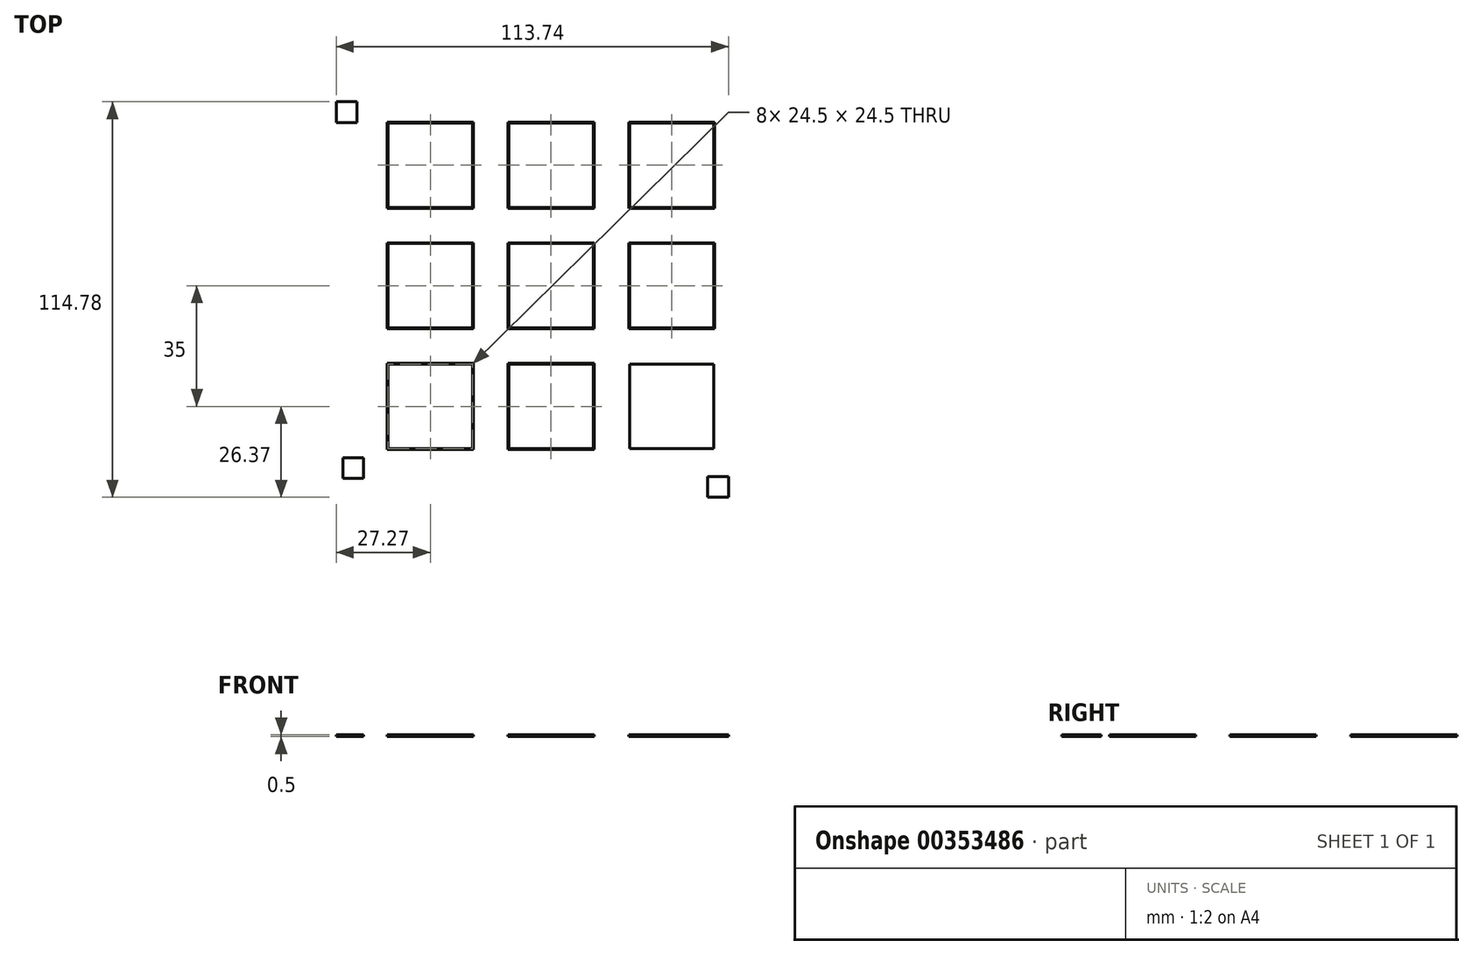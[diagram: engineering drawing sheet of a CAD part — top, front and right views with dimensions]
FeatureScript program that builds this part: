
annotation { "Feature Type Name" : "Feature", "Feature Type Description" : "" }
export const myFeature = defineFeature(function(context is Context, id is Id, definition is map)
    precondition{}
    {
        {
            var Q0;
            Q0=qCreatedBy(makeId("Top.planeOp"),FACE);
            var sketch = newSketch(context, id + "F0", { "sketchPlane" : qUnion([Q0])});
            skLineSegment(sketch, "E0.bottom", {"start": v(-22.5, -12.5) * mm, "end": v(-47.5, -12.5) * mm});
            skLineSegment(sketch, "E0.top", {"start": v(-22.5, 12.5) * mm, "end": v(-47.5, 12.5) * mm});
            skLineSegment(sketch, "E0.left", {"start": v(-22.5, -12.5) * mm, "end": v(-22.5, 12.5) * mm});
            skLineSegment(sketch, "E0.right", {"start": v(-47.5, -12.5) * mm, "end": v(-47.5, 12.5) * mm});
            skPoint(sketch, "E0.middle", {"position": v(-35, 0) * mm});
            skLineSegment(sketch, "E1.bottom", {"start": v(-47.25, 12.25) * mm, "end": v(-22.75, 12.25) * mm});
            skLineSegment(sketch, "E1.top", {"start": v(-47.25, -12.25) * mm, "end": v(-22.75, -12.25) * mm});
            skLineSegment(sketch, "E1.left", {"start": v(-47.25, 12.25) * mm, "end": v(-47.25, -12.25) * mm});
            skLineSegment(sketch, "E1.right", {"start": v(-22.75, 12.25) * mm, "end": v(-22.75, -12.25) * mm});
            skLineSegment(sketch, "E2.bottom", {"start": v(12.5, 22.5) * mm, "end": v(-12.5, 22.5) * mm});
            skLineSegment(sketch, "E2.top", {"start": v(12.5, 47.5) * mm, "end": v(-12.5, 47.5) * mm});
            skLineSegment(sketch, "E2.left", {"start": v(12.5, 22.5) * mm, "end": v(12.5, 47.5) * mm});
            skLineSegment(sketch, "E2.right", {"start": v(-12.5, 22.5) * mm, "end": v(-12.5, 47.5) * mm});
            skPoint(sketch, "E2.middle", {"position": v(0, 35) * mm});
            skLineSegment(sketch, "E3.bottom", {"start": v(-12.25, 47.25) * mm, "end": v(12.25, 47.25) * mm});
            skLineSegment(sketch, "E3.top", {"start": v(-12.25, 22.75) * mm, "end": v(12.25, 22.75) * mm});
            skLineSegment(sketch, "E3.left", {"start": v(-12.25, 47.25) * mm, "end": v(-12.25, 22.75) * mm});
            skLineSegment(sketch, "E3.right", {"start": v(12.25, 47.25) * mm, "end": v(12.25, 22.75) * mm});
            skLineSegment(sketch, "E4.bottom", {"start": v(-22.5, 22.5) * mm, "end": v(-47.5, 22.5) * mm});
            skLineSegment(sketch, "E4.top", {"start": v(-22.5, 47.5) * mm, "end": v(-47.5, 47.5) * mm});
            skLineSegment(sketch, "E4.left", {"start": v(-22.5, 22.5) * mm, "end": v(-22.5, 47.5) * mm});
            skLineSegment(sketch, "E4.right", {"start": v(-47.5, 22.5) * mm, "end": v(-47.5, 47.5) * mm});
            skPoint(sketch, "E4.middle", {"position": v(-35, 35) * mm});
            skLineSegment(sketch, "E5.bottom", {"start": v(-47.25, 47.25) * mm, "end": v(-22.75, 47.25) * mm});
            skLineSegment(sketch, "E5.top", {"start": v(-47.25, 22.75) * mm, "end": v(-22.75, 22.75) * mm});
            skLineSegment(sketch, "E5.left", {"start": v(-47.25, 47.25) * mm, "end": v(-47.25, 22.75) * mm});
            skLineSegment(sketch, "E5.right", {"start": v(-22.75, 47.25) * mm, "end": v(-22.75, 22.75) * mm});
            skLineSegment(sketch, "E6.bottom", {"start": v(12.5, -12.5) * mm, "end": v(-12.5, -12.5) * mm});
            skLineSegment(sketch, "E6.top", {"start": v(12.5, 12.5) * mm, "end": v(-12.5, 12.5) * mm});
            skLineSegment(sketch, "E6.left", {"start": v(12.5, -12.5) * mm, "end": v(12.5, 12.5) * mm});
            skLineSegment(sketch, "E6.right", {"start": v(-12.5, -12.5) * mm, "end": v(-12.5, 12.5) * mm});
            skPoint(sketch, "E6.middle", {"position": v(0, 0) * mm});
            skLineSegment(sketch, "E7.bottom", {"start": v(-12.25, 12.25) * mm, "end": v(12.25, 12.25) * mm});
            skLineSegment(sketch, "E7.top", {"start": v(-12.25, -12.25) * mm, "end": v(12.25, -12.25) * mm});
            skLineSegment(sketch, "E7.left", {"start": v(-12.25, 12.25) * mm, "end": v(-12.25, -12.25) * mm});
            skLineSegment(sketch, "E7.right", {"start": v(12.25, 12.25) * mm, "end": v(12.25, -12.25) * mm});
            skLineSegment(sketch, "E8.bottom", {"start": v(-22.5, -47.5) * mm, "end": v(-47.5, -47.5) * mm});
            skLineSegment(sketch, "E8.top", {"start": v(-22.5, -22.5) * mm, "end": v(-47.5, -22.5) * mm});
            skLineSegment(sketch, "E8.left", {"start": v(-22.5, -47.5) * mm, "end": v(-22.5, -22.5) * mm});
            skLineSegment(sketch, "E8.right", {"start": v(-47.5, -47.5) * mm, "end": v(-47.5, -22.5) * mm});
            skPoint(sketch, "E8.middle", {"position": v(-35, -35) * mm});
            skLineSegment(sketch, "E9.bottom", {"start": v(-47.25, -22.75) * mm, "end": v(-22.75, -22.75) * mm});
            skLineSegment(sketch, "E9.top", {"start": v(-47.25, -47.25) * mm, "end": v(-22.75, -47.25) * mm});
            skLineSegment(sketch, "E9.left", {"start": v(-47.25, -22.75) * mm, "end": v(-47.25, -47.25) * mm});
            skLineSegment(sketch, "E9.right", {"start": v(-22.75, -22.75) * mm, "end": v(-22.75, -47.25) * mm});
            skLineSegment(sketch, "E10.bottom", {"start": v(47.5, -47.5) * mm, "end": v(22.5, -47.5) * mm});
            skLineSegment(sketch, "E10.top", {"start": v(47.5, -22.5) * mm, "end": v(22.5, -22.5) * mm});
            skLineSegment(sketch, "E10.left", {"start": v(-4.53, -59.3) * mm, "end": v(-4.53, -34.3) * mm});
            skLineSegment(sketch, "E10.right", {"start": v(22.5, -47.5) * mm, "end": v(22.5, -22.5) * mm});
            skPoint(sketch, "E10.middle", {"position": v(35, -35) * mm});
            skLineSegment(sketch, "E11.bottom", {"start": v(22.75, -22.75) * mm, "end": v(47.25, -22.75) * mm});
            skLineSegment(sketch, "E11.top", {"start": v(22.75, -47.25) * mm, "end": v(47.25, -47.25) * mm});
            skLineSegment(sketch, "E11.left", {"start": v(22.75, -22.75) * mm, "end": v(22.75, -47.25) * mm});
            skLineSegment(sketch, "E11.right", {"start": v(47.25, -22.75) * mm, "end": v(47.25, -47.25) * mm});
            skLineSegment(sketch, "E12.bottom", {"start": v(12.5, -47.5) * mm, "end": v(-12.5, -47.5) * mm});
            skLineSegment(sketch, "E12.top", {"start": v(12.5, -22.5) * mm, "end": v(-12.5, -22.5) * mm});
            skLineSegment(sketch, "E12.left", {"start": v(12.5, -47.5) * mm, "end": v(12.5, -22.5) * mm});
            skLineSegment(sketch, "E12.right", {"start": v(-12.5, -47.5) * mm, "end": v(-12.5, -22.5) * mm});
            skPoint(sketch, "E12.middle", {"position": v(0, -35) * mm});
            skLineSegment(sketch, "E13.bottom", {"start": v(-12.25, -22.75) * mm, "end": v(12.25, -22.75) * mm});
            skLineSegment(sketch, "E13.top", {"start": v(-12.25, -47.25) * mm, "end": v(12.25, -47.25) * mm});
            skLineSegment(sketch, "E13.left", {"start": v(-12.25, -22.75) * mm, "end": v(-12.25, -47.25) * mm});
            skLineSegment(sketch, "E13.right", {"start": v(12.25, -22.75) * mm, "end": v(12.25, -47.25) * mm});
            skLineSegment(sketch, "E14.bottom", {"start": v(47.5, 22.5) * mm, "end": v(22.5, 22.5) * mm});
            skLineSegment(sketch, "E14.top", {"start": v(47.5, 47.5) * mm, "end": v(22.5, 47.5) * mm});
            skLineSegment(sketch, "E14.left", {"start": v(47.5, 22.5) * mm, "end": v(47.5, 47.5) * mm});
            skLineSegment(sketch, "E14.right", {"start": v(22.5, 22.5) * mm, "end": v(22.5, 47.5) * mm});
            skPoint(sketch, "E14.middle", {"position": v(35, 35) * mm});
            skLineSegment(sketch, "E15.bottom", {"start": v(22.75, 47.25) * mm, "end": v(47.25, 47.25) * mm});
            skLineSegment(sketch, "E15.top", {"start": v(22.75, 22.75) * mm, "end": v(47.25, 22.75) * mm});
            skLineSegment(sketch, "E15.left", {"start": v(22.75, 47.25) * mm, "end": v(22.75, 22.75) * mm});
            skLineSegment(sketch, "E15.right", {"start": v(47.25, 47.25) * mm, "end": v(47.25, 22.75) * mm});
            skLineSegment(sketch, "E16.bottom", {"start": v(47.5, -12.5) * mm, "end": v(22.5, -12.5) * mm});
            skLineSegment(sketch, "E16.top", {"start": v(47.5, 12.5) * mm, "end": v(22.5, 12.5) * mm});
            skLineSegment(sketch, "E16.left", {"start": v(47.5, -12.5) * mm, "end": v(47.5, 12.5) * mm});
            skLineSegment(sketch, "E16.right", {"start": v(22.5, -12.5) * mm, "end": v(22.5, 12.5) * mm});
            skPoint(sketch, "E16.middle", {"position": v(35, 0) * mm});
            skLineSegment(sketch, "E17.bottom", {"start": v(22.75, 12.25) * mm, "end": v(47.25, 12.25) * mm});
            skLineSegment(sketch, "E17.top", {"start": v(22.75, -12.25) * mm, "end": v(47.25, -12.25) * mm});
            skLineSegment(sketch, "E17.left", {"start": v(22.75, 12.25) * mm, "end": v(22.75, -12.25) * mm});
            skLineSegment(sketch, "E17.right", {"start": v(47.25, 12.25) * mm, "end": v(47.25, -12.25) * mm});
            skLineSegment(sketch, "E18.bottom", {"start": v(3, 3) * mm, "end": v(-3, 3) * mm});
            skLineSegment(sketch, "E18.top", {"start": v(3, -3) * mm, "end": v(-3, -3) * mm});
            skLineSegment(sketch, "E18.left", {"start": v(3, 3) * mm, "end": v(3, -3) * mm});
            skLineSegment(sketch, "E18.right", {"start": v(-3, 3) * mm, "end": v(-3, -3) * mm});
            skLineSegment(sketch, "E19.bottom", {"start": v(2.95, 1.94) * mm, "end": v(-2.95, 1.94) * mm});
            skLineSegment(sketch, "E19.top", {"start": v(2.95, -1.94) * mm, "end": v(-2.95, -1.94) * mm});
            skLineSegment(sketch, "E19.left", {"start": v(2.95, 1.94) * mm, "end": v(2.95, -1.94) * mm});
            skLineSegment(sketch, "E19.right", {"start": v(-2.95, 1.94) * mm, "end": v(-2.95, -1.94) * mm});
            skLineSegment(sketch, "E20.bottom", {"start": v(38.25, 3) * mm, "end": v(32.25, 3) * mm});
            skLineSegment(sketch, "E20.top", {"start": v(38.25, -3) * mm, "end": v(32.25, -3) * mm});
            skLineSegment(sketch, "E20.left", {"start": v(38.25, 3) * mm, "end": v(38.25, -3) * mm});
            skLineSegment(sketch, "E20.right", {"start": v(32.25, 3) * mm, "end": v(32.25, -3) * mm});
            skPoint(sketch, "E20.middle", {"position": v(35.25, 0) * mm});
            skLineSegment(sketch, "E21.bottom", {"start": v(-38.25, 3) * mm, "end": v(-32.25, 3) * mm});
            skLineSegment(sketch, "E21.top", {"start": v(-38.25, -3) * mm, "end": v(-32.25, -3) * mm});
            skLineSegment(sketch, "E21.left", {"start": v(-38.25, 3) * mm, "end": v(-38.25, -3) * mm});
            skLineSegment(sketch, "E21.right", {"start": v(-32.25, 3) * mm, "end": v(-32.25, -3) * mm});
            skPoint(sketch, "E21.middle", {"position": v(-35.25, 0) * mm});
            skLineSegment(sketch, "E22.bottom", {"start": v(-3, -38.25) * mm, "end": v(3, -38.25) * mm});
            skLineSegment(sketch, "E22.top", {"start": v(-3, -32.25) * mm, "end": v(3, -32.25) * mm});
            skLineSegment(sketch, "E22.left", {"start": v(-3, -38.25) * mm, "end": v(-3, -32.25) * mm});
            skLineSegment(sketch, "E22.right", {"start": v(3, -38.25) * mm, "end": v(3, -32.25) * mm});
            skPoint(sketch, "E22.middle", {"position": v(0, -35.25) * mm});
            skLineSegment(sketch, "E23.bottom", {"start": v(-3, 38.25) * mm, "end": v(3, 38.25) * mm});
            skLineSegment(sketch, "E23.top", {"start": v(-3, 32.25) * mm, "end": v(3, 32.25) * mm});
            skLineSegment(sketch, "E23.left", {"start": v(-3, 38.25) * mm, "end": v(-3, 32.25) * mm});
            skLineSegment(sketch, "E23.right", {"start": v(3, 38.25) * mm, "end": v(3, 32.25) * mm});
            skPoint(sketch, "E23.middle", {"position": v(0, 35.25) * mm});
            skLineSegment(sketch, "E24.bottom", {"start": v(-62.27, 53.4) * mm, "end": v(-56.27, 53.4) * mm});
            skLineSegment(sketch, "E24.top", {"start": v(-62.27, 47.4) * mm, "end": v(-56.27, 47.4) * mm});
            skLineSegment(sketch, "E24.left", {"start": v(-62.27, 53.4) * mm, "end": v(-62.27, 47.4) * mm});
            skLineSegment(sketch, "E24.right", {"start": v(-56.27, 53.4) * mm, "end": v(-56.27, 47.4) * mm});
            skPoint(sketch, "E24.middle", {"position": v(-59.27, 50.4) * mm});
            skLineSegment(sketch, "E25.bottom", {"start": v(-60.38, -49.86) * mm, "end": v(-54.38, -49.86) * mm});
            skLineSegment(sketch, "E25.top", {"start": v(-60.38, -55.86) * mm, "end": v(-54.38, -55.86) * mm});
            skLineSegment(sketch, "E25.left", {"start": v(-60.38, -49.86) * mm, "end": v(-60.38, -55.86) * mm});
            skLineSegment(sketch, "E25.right", {"start": v(-54.38, -49.86) * mm, "end": v(-54.38, -55.86) * mm});
            skPoint(sketch, "E25.middle", {"position": v(-57.38, -52.86) * mm});
            skLineSegment(sketch, "E26.bottom", {"start": v(45.47, -55.37) * mm, "end": v(51.47, -55.37) * mm});
            skLineSegment(sketch, "E26.top", {"start": v(45.47, -61.37) * mm, "end": v(51.47, -61.37) * mm});
            skLineSegment(sketch, "E26.left", {"start": v(45.47, -55.37) * mm, "end": v(45.47, -61.37) * mm});
            skLineSegment(sketch, "E26.right", {"start": v(51.47, -55.37) * mm, "end": v(51.47, -61.37) * mm});
            skPoint(sketch, "E26.middle", {"position": v(48.47, -58.37) * mm});
            skLineSegment(sketch, "E27.bottom", {"start": v(32.5, 38.5) * mm, "end": v(38.5, 38.5) * mm});
            skLineSegment(sketch, "E27.top", {"start": v(32.5, 32.5) * mm, "end": v(38.5, 32.5) * mm});
            skLineSegment(sketch, "E27.left", {"start": v(32.5, 38.5) * mm, "end": v(32.5, 32.5) * mm});
            skLineSegment(sketch, "E27.right", {"start": v(38.5, 38.5) * mm, "end": v(38.5, 32.5) * mm});
            skPoint(sketch, "E27.middle", {"position": v(35.5, 35.5) * mm});
            skSolve(sketch);
        }
        {
            var Q0;
            Q0 = qSketchRegion(id + "F0", true);
            extrude(context, id + "F1", {"entities" : qUnion([Q0]), "depth" : .5 * mm});
        }
    });
